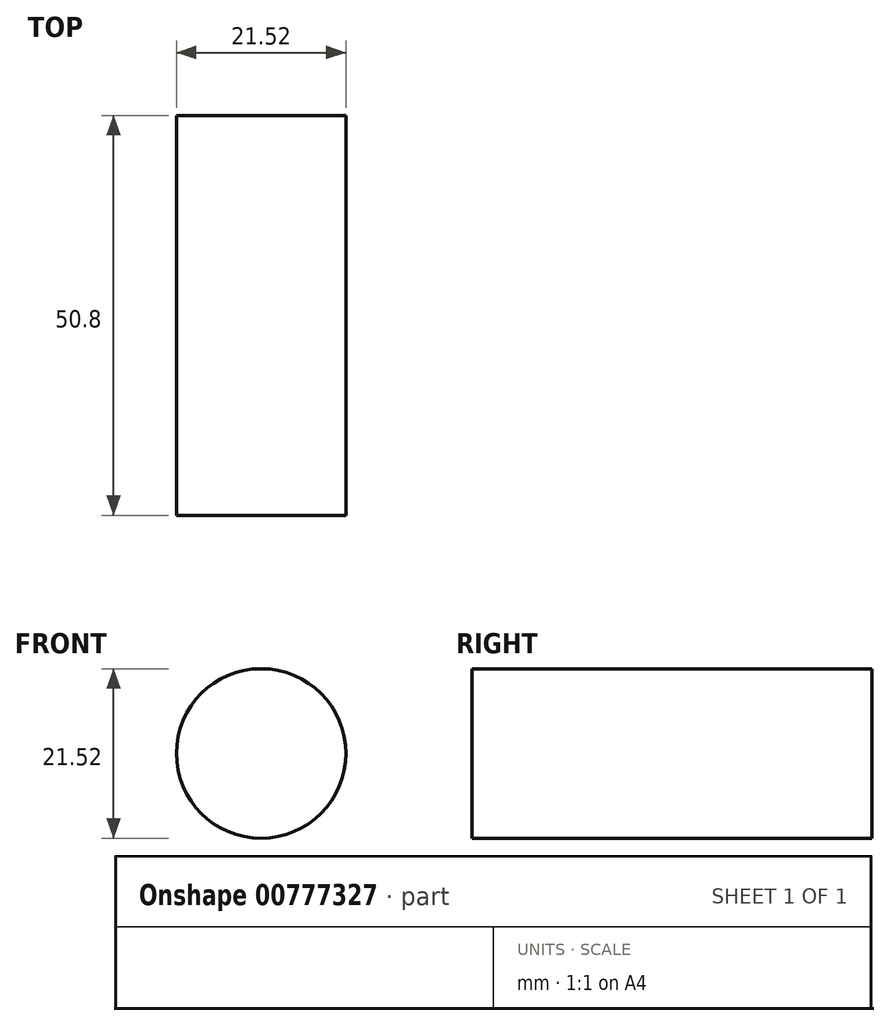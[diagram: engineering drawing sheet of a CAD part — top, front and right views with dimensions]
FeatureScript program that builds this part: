
annotation { "Feature Type Name" : "Feature", "Feature Type Description" : "" }
export const myFeature = defineFeature(function(context is Context, id is Id, definition is map)
    precondition{}
    {
        {
            var Q0;
            Q0=qCreatedBy(makeId("Front.planeOp"),FACE);
            var sketch = newSketch(context, id + "F0", { "sketchPlane" : qUnion([Q0])});
            skCircle(sketch, "E0", {"center": v(0, 0) * mm, "radius": 26.69 * mm});
            skCircle(sketch, "E1", {"center": v(0, 0) * mm, "radius": 40.97 * mm});
            skCircle(sketch, "E2", {"center": v(0, 0) * mm, "radius": 73.84 * mm});
            skCircle(sketch, "E3", {"center": v(-151.82, 0) * mm, "radius": 48.92 * mm});
            skCircle(sketch, "E4", {"center": v(-151.82, 0) * mm, "radius": 37.5 * mm});
            skCircle(sketch, "E5", {"center": v(0, 0) * mm, "radius": 10.76 * mm});
            skCircle(sketch, "E6", {"center": v(0, 0) * mm, "radius": 17.44 * mm});
            skSolve(sketch);
        }
        {
            var Q0;
            Q0=makeQuery(id+"F0.imprint","IMPRINT",FACE,{"disambiguationData":[TD([[makeQuery(id+"F0.imprint","IMPRINT",EDGE,{"derivedFrom":sQuery(id+"F0.wireOp",EDGE,"E5")}),1.0]])]});
            extrude(context, id + "F1", {"entities" : qUnion([Q0]), "oppositeDirection" : true, "depth" : 50.8 * mm, "offsetDistance" : 25.4 * mm});
        }
    });
